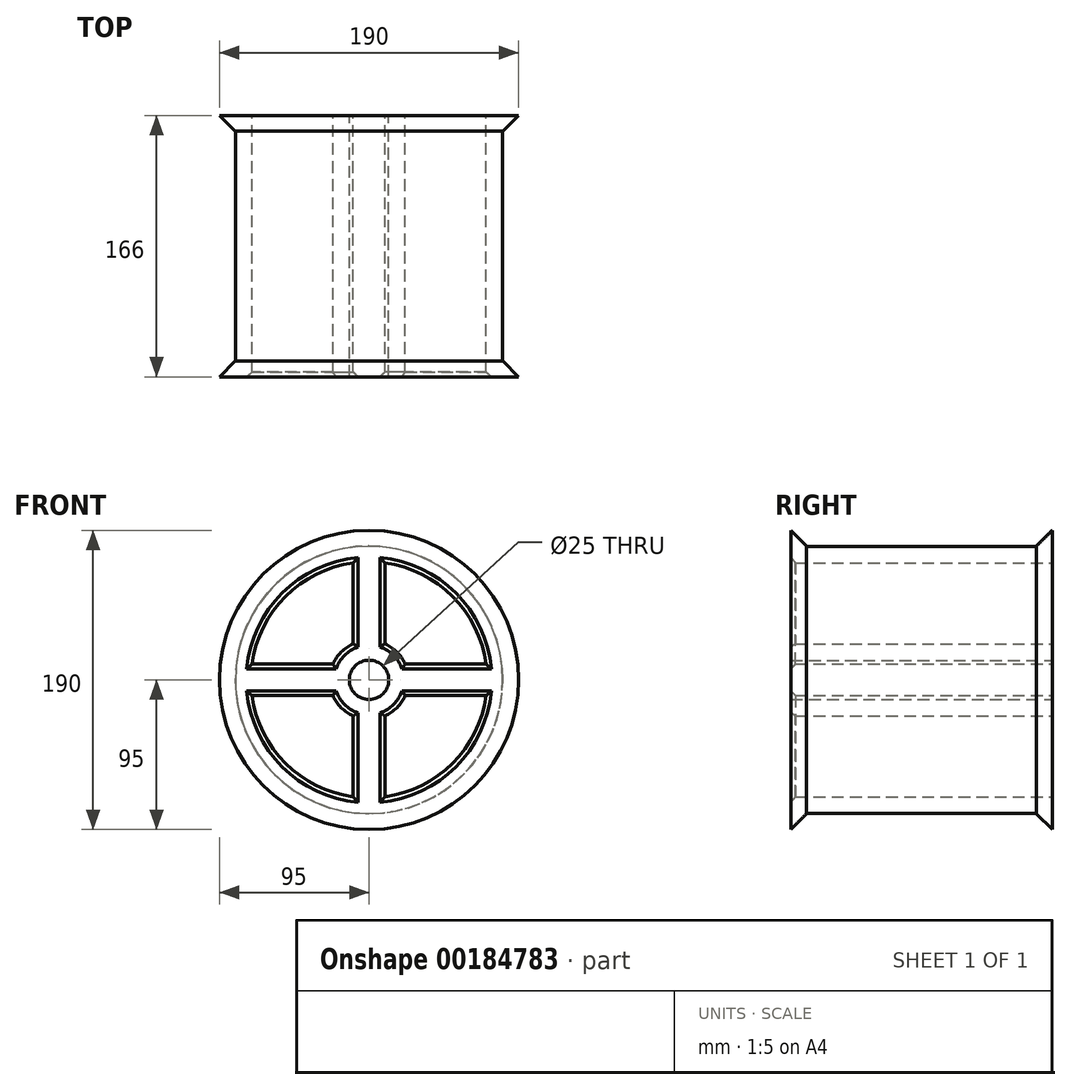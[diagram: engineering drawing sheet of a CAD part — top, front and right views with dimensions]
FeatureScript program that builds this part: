
annotation { "Feature Type Name" : "Feature", "Feature Type Description" : "" }
export const myFeature = defineFeature(function(context is Context, id is Id, definition is map)
    precondition{}
    {
        {
            var Q0;
            Q0=qCreatedBy(makeId("Front.planeOp"),FACE);
            var sketch = newSketch(context, id + "F0", { "sketchPlane" : qUnion([Q0])});
            skCircle(sketch, "E0", {"center": v(0, 0) * mm, "radius": 84.9 * mm});
            skSolve(sketch);
        }
        {
            var Q0;
            Q0=makeQuery(id+"F0.imprint","IMPRINT",FACE,{"disambiguationData":[TD([[makeQuery(id+"F0.imprint","IMPRINT",EDGE,{"derivedFrom":sQuery(id+"F0.wireOp",EDGE,"E0")}),1.0]])]});
            extrude(context, id + "F1", {"entities" : qUnion([Q0]), "depth" : 166 * mm});
        }
        {
            var Q0;
            Q0=makeQuery(id+"F1.opExtrude","CAP_FACE",FACE,{"disambiguationData":[OSD([sQuery(id+"F0.wireOp",EDGE,"E0")])],"isStart":true});
            var sketch = newSketch(context, id + "F2", { "sketchPlane" : qUnion([Q0])});
            skCircle(sketch, "E1", {"center": v(0, 0) * mm, "radius": 95 * mm});
            skSolve(sketch);
        }
        {
            var Q0;
            Q0=makeQuery(id+"F2.imprint","IMPRINT",FACE,{"disambiguationData":[TD([[makeQuery(id+"F2.imprint","IMPRINT",EDGE,{"derivedFrom":sQuery(id+"F2.wireOp",EDGE,"E1")}),1.0]])]});
            var Q1;
            Q1=sQuery(id+"F2.wireOp",EDGE,"E1");
            extrude(context, id + "F3", {"entities" : qUnion([Q0]), "operationType" : NewBodyOperationType.ADD, "surfaceEntities" : qUnion([Q1]), "oppositeDirection" : true, "depth" : 10 * mm});
        }
        {
            var Q0;
            Q0=makeQuery(id+"F1.opExtrude","CAP_FACE",FACE,{"disambiguationData":[OSD([sQuery(id+"F0.wireOp",EDGE,"E0")])],"isStart":false});
            var sketch = newSketch(context, id + "F4", { "sketchPlane" : qUnion([Q0])});
            skCircle(sketch, "E2", {"center": v(0, 0) * mm, "radius": 95 * mm});
            skSolve(sketch);
        }
        {
            var Q0;
            Q0=makeQuery(id+"F4.imprint","IMPRINT",FACE,{"disambiguationData":[TD([[makeQuery(id+"F4.imprint","IMPRINT",EDGE,{"derivedFrom":sQuery(id+"F4.wireOp",EDGE,"E2")}),1.0]])]});
            var Q1;
            Q1=sQuery(id+"F4.wireOp",EDGE,"E2");
            extrude(context, id + "F5", {"entities" : qUnion([Q0]), "operationType" : NewBodyOperationType.ADD, "surfaceEntities" : qUnion([Q1]), "oppositeDirection" : true, "depth" : 10 * mm});
        }
        {
            var Q0;
            Q0=makeQuery(id+"F3.opExtrude","CAP_EDGE",EDGE,{"disambiguationData":[OSD([sQuery(id+"F2.wireOp",EDGE,"E1")])],"isStart":false});
            var Q1;
            Q1=makeQuery(id+"F5.opExtrude","CAP_EDGE",EDGE,{"disambiguationData":[OSD([sQuery(id+"F4.wireOp",EDGE,"E2")])],"isStart":false});
            chamfer(context, id + "F6", {"entities" : qUnion([Q0, Q1]), "width" : 10 * mm, "tangentPropagation" : true});
        }
        {
            var Q0;
            {var subQ0=sQuery(id+"F0.wireOp",EDGE,"E0");Q0=makeQuery(id+"F3.boolean.opBoolean","MERGE",FACE,{"derivedFrom":[makeQuery(id+"F1.opExtrude","CAP_FACE",FACE,{"disambiguationData":[OSD([subQ0])],"isStart":true}),makeQuery(id+"F3.opExtrude","CAP_FACE",FACE,{"disambiguationData":[OSD([subQ0,sQuery(id+"F2.wireOp",EDGE,"E1")])],"isStart":true})]});}
            var sketch = newSketch(context, id + "F7", { "sketchPlane" : qUnion([Q0])});
            skCircle(sketch, "E3", {"center": v(0, 0) * mm, "radius": 75 * mm});
            skCircle(sketch, "E4", {"center": v(0, 0) * mm, "radius": 25 * mm});
            skCircle(sketch, "E5", {"center": v(0, 0) * mm, "radius": 12.5 * mm});
            skLineSegment(sketch, "E6", {"start": v(25, 0) * mm, "end": v(75, 0) * mm});
            skLineSegment(sketch, "E7", {"start": v(-25, 0) * mm, "end": v(-75, 0) * mm});
            skLineSegment(sketch, "E8", {"start": v(0, -25) * mm, "end": v(0, -75) * mm});
            skLineSegment(sketch, "E9", {"start": v(0, 25) * mm, "end": v(0, 75) * mm});
            skLineSegment(sketch, "E10", {"start": v(-22.91, 10) * mm, "end": v(-74.33, 10) * mm});
            skLineSegment(sketch, "E11", {"start": v(-22.91, -10) * mm, "end": v(-74.33, -10) * mm});
            skLineSegment(sketch, "E12", {"start": v(-10, -22.91) * mm, "end": v(-10, -74.33) * mm});
            skLineSegment(sketch, "E13", {"start": v(10, -22.91) * mm, "end": v(10, -74.33) * mm});
            skLineSegment(sketch, "E14", {"start": v(22.91, -10) * mm, "end": v(74.33, -10) * mm});
            skLineSegment(sketch, "E15", {"start": v(22.91, 10) * mm, "end": v(74.33, 10) * mm});
            skLineSegment(sketch, "E16", {"start": v(10, 22.91) * mm, "end": v(10, 74.33) * mm});
            skLineSegment(sketch, "E17", {"start": v(-10, 22.91) * mm, "end": v(-10, 74.33) * mm});
            skSolve(sketch);
        }
        {
            var Q0;
            {var subQ0=sQuery(id+"F7.wireOp",EDGE,"E10");Q0=makeQuery(id+"F7.imprint","IMPRINT",FACE,{"disambiguationData":[TD([[makeQuery(id+"F7.imprint","IMPRINT",EDGE,{"derivedFrom":subQ0}),-1.0]])]});}
            var Q1;
            {var subQ0=sQuery(id+"F7.wireOp",EDGE,"E15");Q1=makeQuery(id+"F7.imprint","IMPRINT",FACE,{"disambiguationData":[TD([[makeQuery(id+"F7.imprint","IMPRINT",EDGE,{"derivedFrom":subQ0}),1.0]])]});}
            var Q2;
            {var subQ0=sQuery(id+"F7.wireOp",EDGE,"E11");Q2=makeQuery(id+"F7.imprint","IMPRINT",FACE,{"disambiguationData":[TD([[makeQuery(id+"F7.imprint","IMPRINT",EDGE,{"derivedFrom":subQ0}),1.0]])]});}
            var Q3;
            {var subQ0=sQuery(id+"F7.wireOp",EDGE,"E13");Q3=makeQuery(id+"F7.imprint","IMPRINT",FACE,{"disambiguationData":[TD([[makeQuery(id+"F7.imprint","IMPRINT",EDGE,{"derivedFrom":subQ0}),1.0]])]});}
            var Q4;
            Q4=makeQuery(id+"F7.imprint","IMPRINT",FACE,{"disambiguationData":[TD([[makeQuery(id+"F7.imprint","IMPRINT",EDGE,{"derivedFrom":sQuery(id+"F7.wireOp",EDGE,"E5")}),1.0]])]});
            extrude(context, id + "F8", {"entities" : qUnion([Q0, Q1, Q2, Q3, Q4]), "operationType" : NewBodyOperationType.REMOVE, "endBound" : BoundingType.THROUGH_ALL, "oppositeDirection" : true, "depth" : 25.4 * mm});
        }
        {
            var Q0;
            {var subQ0=sQuery(id+"F7.wireOp",EDGE,"E3");var subQ1=sQuery(id+"F0.wireOp",EDGE,"E0");Q0=makeQuery(id+"F8.boolean.opBoolean","INTERSECT",EDGE,{"derivedFrom":[makeQuery(id+"F5.boolean.opBoolean","MERGE",FACE,{"derivedFrom":[makeQuery(id+"F1.opExtrude","CAP_FACE",FACE,{"disambiguationData":[OSD([subQ1])],"isStart":false}),makeQuery(id+"F5.opExtrude","CAP_FACE",FACE,{"disambiguationData":[OSD([subQ1,sQuery(id+"F4.wireOp",EDGE,"E2")])],"isStart":true})]}),makeQuery(id+"F8.opExtrude","SWEPT_FACE",FACE,{"disambiguationData":[OSD([subQ0]),TDD([makeQuery(id+"F7.imprint","IMPRINT",EDGE,{"disambiguationData":[TD([[makeQuery(id+"F7.imprint","INTERSECT",VERTEX,{"derivedFrom":[subQ0,sQuery(id+"F7.wireOp",EDGE,"E15")]}),-1.0]])],"derivedFrom":subQ0})])]})]});}
            var Q1;
            {var subQ0=sQuery(id+"F0.wireOp",EDGE,"E0");Q1=makeQuery(id+"F8.boolean.opBoolean","INTERSECT",EDGE,{"derivedFrom":[makeQuery(id+"F5.boolean.opBoolean","MERGE",FACE,{"derivedFrom":[makeQuery(id+"F1.opExtrude","CAP_FACE",FACE,{"disambiguationData":[OSD([subQ0])],"isStart":false}),makeQuery(id+"F5.opExtrude","CAP_FACE",FACE,{"disambiguationData":[OSD([subQ0,sQuery(id+"F4.wireOp",EDGE,"E2")])],"isStart":true})]}),makeQuery(id+"F8.opExtrude","SWEPT_FACE",FACE,{"disambiguationData":[OSD([sQuery(id+"F7.wireOp",EDGE,"E16")])]})]});}
            var Q2;
            {var subQ0=sQuery(id+"F0.wireOp",EDGE,"E0");Q2=makeQuery(id+"F8.boolean.opBoolean","INTERSECT",EDGE,{"derivedFrom":[makeQuery(id+"F5.boolean.opBoolean","MERGE",FACE,{"derivedFrom":[makeQuery(id+"F1.opExtrude","CAP_FACE",FACE,{"disambiguationData":[OSD([subQ0])],"isStart":false}),makeQuery(id+"F5.opExtrude","CAP_FACE",FACE,{"disambiguationData":[OSD([subQ0,sQuery(id+"F4.wireOp",EDGE,"E2")])],"isStart":true})]}),makeQuery(id+"F8.opExtrude","SWEPT_FACE",FACE,{"disambiguationData":[OSD([sQuery(id+"F7.wireOp",EDGE,"E15")])]})]});}
            var Q3;
            {var subQ0=sQuery(id+"F7.wireOp",EDGE,"E4");var subQ1=sQuery(id+"F0.wireOp",EDGE,"E0");Q3=makeQuery(id+"F8.boolean.opBoolean","INTERSECT",EDGE,{"derivedFrom":[makeQuery(id+"F5.boolean.opBoolean","MERGE",FACE,{"derivedFrom":[makeQuery(id+"F1.opExtrude","CAP_FACE",FACE,{"disambiguationData":[OSD([subQ1])],"isStart":false}),makeQuery(id+"F5.opExtrude","CAP_FACE",FACE,{"disambiguationData":[OSD([subQ1,sQuery(id+"F4.wireOp",EDGE,"E2")])],"isStart":true})]}),makeQuery(id+"F8.opExtrude","SWEPT_FACE",FACE,{"disambiguationData":[OSD([subQ0]),TDD([makeQuery(id+"F7.imprint","IMPRINT",EDGE,{"disambiguationData":[TD([[makeQuery(id+"F7.imprint","INTERSECT",VERTEX,{"derivedFrom":[subQ0,sQuery(id+"F7.wireOp",EDGE,"E15")]}),-1.0]])],"derivedFrom":subQ0})])]})]});}
            var Q4;
            {var subQ0=sQuery(id+"F7.wireOp",EDGE,"E3");var subQ1=sQuery(id+"F0.wireOp",EDGE,"E0");Q4=makeQuery(id+"F8.boolean.opBoolean","INTERSECT",EDGE,{"derivedFrom":[makeQuery(id+"F5.boolean.opBoolean","MERGE",FACE,{"derivedFrom":[makeQuery(id+"F1.opExtrude","CAP_FACE",FACE,{"disambiguationData":[OSD([subQ1])],"isStart":false}),makeQuery(id+"F5.opExtrude","CAP_FACE",FACE,{"disambiguationData":[OSD([subQ1,sQuery(id+"F4.wireOp",EDGE,"E2")])],"isStart":true})]}),makeQuery(id+"F8.opExtrude","SWEPT_FACE",FACE,{"disambiguationData":[OSD([subQ0]),TDD([makeQuery(id+"F7.imprint","IMPRINT",EDGE,{"disambiguationData":[TD([[makeQuery(id+"F7.imprint","INTERSECT",VERTEX,{"derivedFrom":[subQ0,sQuery(id+"F7.wireOp",EDGE,"E10")]}),1.0]])],"derivedFrom":subQ0})])]})]});}
            var Q5;
            {var subQ0=sQuery(id+"F0.wireOp",EDGE,"E0");Q5=makeQuery(id+"F8.boolean.opBoolean","INTERSECT",EDGE,{"derivedFrom":[makeQuery(id+"F5.boolean.opBoolean","MERGE",FACE,{"derivedFrom":[makeQuery(id+"F1.opExtrude","CAP_FACE",FACE,{"disambiguationData":[OSD([subQ0])],"isStart":false}),makeQuery(id+"F5.opExtrude","CAP_FACE",FACE,{"disambiguationData":[OSD([subQ0,sQuery(id+"F4.wireOp",EDGE,"E2")])],"isStart":true})]}),makeQuery(id+"F8.opExtrude","SWEPT_FACE",FACE,{"disambiguationData":[OSD([sQuery(id+"F7.wireOp",EDGE,"E10")])]})]});}
            var Q6;
            {var subQ0=sQuery(id+"F7.wireOp",EDGE,"E4");var subQ1=sQuery(id+"F0.wireOp",EDGE,"E0");Q6=makeQuery(id+"F8.boolean.opBoolean","INTERSECT",EDGE,{"derivedFrom":[makeQuery(id+"F5.boolean.opBoolean","MERGE",FACE,{"derivedFrom":[makeQuery(id+"F1.opExtrude","CAP_FACE",FACE,{"disambiguationData":[OSD([subQ1])],"isStart":false}),makeQuery(id+"F5.opExtrude","CAP_FACE",FACE,{"disambiguationData":[OSD([subQ1,sQuery(id+"F4.wireOp",EDGE,"E2")])],"isStart":true})]}),makeQuery(id+"F8.opExtrude","SWEPT_FACE",FACE,{"disambiguationData":[OSD([subQ0]),TDD([makeQuery(id+"F7.imprint","IMPRINT",EDGE,{"disambiguationData":[TD([[makeQuery(id+"F7.imprint","INTERSECT",VERTEX,{"derivedFrom":[subQ0,sQuery(id+"F7.wireOp",EDGE,"E10")]}),1.0]])],"derivedFrom":subQ0})])]})]});}
            var Q7;
            {var subQ0=sQuery(id+"F0.wireOp",EDGE,"E0");Q7=makeQuery(id+"F8.boolean.opBoolean","INTERSECT",EDGE,{"derivedFrom":[makeQuery(id+"F5.boolean.opBoolean","MERGE",FACE,{"derivedFrom":[makeQuery(id+"F1.opExtrude","CAP_FACE",FACE,{"disambiguationData":[OSD([subQ0])],"isStart":false}),makeQuery(id+"F5.opExtrude","CAP_FACE",FACE,{"disambiguationData":[OSD([subQ0,sQuery(id+"F4.wireOp",EDGE,"E2")])],"isStart":true})]}),makeQuery(id+"F8.opExtrude","SWEPT_FACE",FACE,{"disambiguationData":[OSD([sQuery(id+"F7.wireOp",EDGE,"E17")])]})]});}
            var Q8;
            {var subQ0=sQuery(id+"F0.wireOp",EDGE,"E0");Q8=makeQuery(id+"F8.boolean.opBoolean","INTERSECT",EDGE,{"derivedFrom":[makeQuery(id+"F5.boolean.opBoolean","MERGE",FACE,{"derivedFrom":[makeQuery(id+"F1.opExtrude","CAP_FACE",FACE,{"disambiguationData":[OSD([subQ0])],"isStart":false}),makeQuery(id+"F5.opExtrude","CAP_FACE",FACE,{"disambiguationData":[OSD([subQ0,sQuery(id+"F4.wireOp",EDGE,"E2")])],"isStart":true})]}),makeQuery(id+"F8.opExtrude","SWEPT_FACE",FACE,{"disambiguationData":[OSD([sQuery(id+"F7.wireOp",EDGE,"E11")])]})]});}
            var Q9;
            {var subQ0=sQuery(id+"F7.wireOp",EDGE,"E3");var subQ1=sQuery(id+"F0.wireOp",EDGE,"E0");Q9=makeQuery(id+"F8.boolean.opBoolean","INTERSECT",EDGE,{"derivedFrom":[makeQuery(id+"F5.boolean.opBoolean","MERGE",FACE,{"derivedFrom":[makeQuery(id+"F1.opExtrude","CAP_FACE",FACE,{"disambiguationData":[OSD([subQ1])],"isStart":false}),makeQuery(id+"F5.opExtrude","CAP_FACE",FACE,{"disambiguationData":[OSD([subQ1,sQuery(id+"F4.wireOp",EDGE,"E2")])],"isStart":true})]}),makeQuery(id+"F8.opExtrude","SWEPT_FACE",FACE,{"disambiguationData":[OSD([subQ0]),TDD([makeQuery(id+"F7.imprint","IMPRINT",EDGE,{"disambiguationData":[TD([[makeQuery(id+"F7.imprint","INTERSECT",VERTEX,{"derivedFrom":[subQ0,sQuery(id+"F7.wireOp",EDGE,"E11")]}),-1.0]])],"derivedFrom":subQ0})])]})]});}
            var Q10;
            {var subQ0=sQuery(id+"F7.wireOp",EDGE,"E4");var subQ1=sQuery(id+"F0.wireOp",EDGE,"E0");Q10=makeQuery(id+"F8.boolean.opBoolean","INTERSECT",EDGE,{"derivedFrom":[makeQuery(id+"F5.boolean.opBoolean","MERGE",FACE,{"derivedFrom":[makeQuery(id+"F1.opExtrude","CAP_FACE",FACE,{"disambiguationData":[OSD([subQ1])],"isStart":false}),makeQuery(id+"F5.opExtrude","CAP_FACE",FACE,{"disambiguationData":[OSD([subQ1,sQuery(id+"F4.wireOp",EDGE,"E2")])],"isStart":true})]}),makeQuery(id+"F8.opExtrude","SWEPT_FACE",FACE,{"disambiguationData":[OSD([subQ0]),TDD([makeQuery(id+"F7.imprint","IMPRINT",EDGE,{"disambiguationData":[TD([[makeQuery(id+"F7.imprint","INTERSECT",VERTEX,{"derivedFrom":[subQ0,sQuery(id+"F7.wireOp",EDGE,"E11")]}),-1.0]])],"derivedFrom":subQ0})])]})]});}
            var Q11;
            {var subQ0=sQuery(id+"F0.wireOp",EDGE,"E0");Q11=makeQuery(id+"F8.boolean.opBoolean","INTERSECT",EDGE,{"derivedFrom":[makeQuery(id+"F5.boolean.opBoolean","MERGE",FACE,{"derivedFrom":[makeQuery(id+"F1.opExtrude","CAP_FACE",FACE,{"disambiguationData":[OSD([subQ0])],"isStart":false}),makeQuery(id+"F5.opExtrude","CAP_FACE",FACE,{"disambiguationData":[OSD([subQ0,sQuery(id+"F4.wireOp",EDGE,"E2")])],"isStart":true})]}),makeQuery(id+"F8.opExtrude","SWEPT_FACE",FACE,{"disambiguationData":[OSD([sQuery(id+"F7.wireOp",EDGE,"E12")])]})]});}
            var Q12;
            {var subQ0=sQuery(id+"F0.wireOp",EDGE,"E0");Q12=makeQuery(id+"F8.boolean.opBoolean","INTERSECT",EDGE,{"derivedFrom":[makeQuery(id+"F5.boolean.opBoolean","MERGE",FACE,{"derivedFrom":[makeQuery(id+"F1.opExtrude","CAP_FACE",FACE,{"disambiguationData":[OSD([subQ0])],"isStart":false}),makeQuery(id+"F5.opExtrude","CAP_FACE",FACE,{"disambiguationData":[OSD([subQ0,sQuery(id+"F4.wireOp",EDGE,"E2")])],"isStart":true})]}),makeQuery(id+"F8.opExtrude","SWEPT_FACE",FACE,{"disambiguationData":[OSD([sQuery(id+"F7.wireOp",EDGE,"E13")])]})]});}
            var Q13;
            {var subQ0=sQuery(id+"F7.wireOp",EDGE,"E4");var subQ1=sQuery(id+"F0.wireOp",EDGE,"E0");Q13=makeQuery(id+"F8.boolean.opBoolean","INTERSECT",EDGE,{"derivedFrom":[makeQuery(id+"F5.boolean.opBoolean","MERGE",FACE,{"derivedFrom":[makeQuery(id+"F1.opExtrude","CAP_FACE",FACE,{"disambiguationData":[OSD([subQ1])],"isStart":false}),makeQuery(id+"F5.opExtrude","CAP_FACE",FACE,{"disambiguationData":[OSD([subQ1,sQuery(id+"F4.wireOp",EDGE,"E2")])],"isStart":true})]}),makeQuery(id+"F8.opExtrude","SWEPT_FACE",FACE,{"disambiguationData":[OSD([subQ0]),TDD([makeQuery(id+"F7.imprint","IMPRINT",EDGE,{"disambiguationData":[TD([[makeQuery(id+"F7.imprint","INTERSECT",VERTEX,{"derivedFrom":[subQ0,sQuery(id+"F7.wireOp",EDGE,"E13")]}),-1.0]])],"derivedFrom":subQ0})])]})]});}
            var Q14;
            {var subQ0=sQuery(id+"F0.wireOp",EDGE,"E0");Q14=makeQuery(id+"F8.boolean.opBoolean","INTERSECT",EDGE,{"derivedFrom":[makeQuery(id+"F5.boolean.opBoolean","MERGE",FACE,{"derivedFrom":[makeQuery(id+"F1.opExtrude","CAP_FACE",FACE,{"disambiguationData":[OSD([subQ0])],"isStart":false}),makeQuery(id+"F5.opExtrude","CAP_FACE",FACE,{"disambiguationData":[OSD([subQ0,sQuery(id+"F4.wireOp",EDGE,"E2")])],"isStart":true})]}),makeQuery(id+"F8.opExtrude","SWEPT_FACE",FACE,{"disambiguationData":[OSD([sQuery(id+"F7.wireOp",EDGE,"E14")])]})]});}
            var Q15;
            {var subQ0=sQuery(id+"F7.wireOp",EDGE,"E3");var subQ1=sQuery(id+"F0.wireOp",EDGE,"E0");Q15=makeQuery(id+"F8.boolean.opBoolean","INTERSECT",EDGE,{"derivedFrom":[makeQuery(id+"F5.boolean.opBoolean","MERGE",FACE,{"derivedFrom":[makeQuery(id+"F1.opExtrude","CAP_FACE",FACE,{"disambiguationData":[OSD([subQ1])],"isStart":false}),makeQuery(id+"F5.opExtrude","CAP_FACE",FACE,{"disambiguationData":[OSD([subQ1,sQuery(id+"F4.wireOp",EDGE,"E2")])],"isStart":true})]}),makeQuery(id+"F8.opExtrude","SWEPT_FACE",FACE,{"disambiguationData":[OSD([subQ0]),TDD([makeQuery(id+"F7.imprint","IMPRINT",EDGE,{"disambiguationData":[TD([[makeQuery(id+"F7.imprint","INTERSECT",VERTEX,{"derivedFrom":[subQ0,sQuery(id+"F7.wireOp",EDGE,"E13")]}),-1.0]])],"derivedFrom":subQ0})])]})]});}
            var Q16;
            {var subQ0=sQuery(id+"F7.wireOp",EDGE,"E3");Q16=makeQuery(id+"F8.boolean.opBoolean","COPY",EDGE,{"derivedFrom":makeQuery(id+"F8.opExtrude","CAP_EDGE",EDGE,{"disambiguationData":[OSD([subQ0]),TDD([makeQuery(id+"F7.imprint","IMPRINT",EDGE,{"disambiguationData":[TD([[makeQuery(id+"F7.imprint","INTERSECT",VERTEX,{"derivedFrom":[subQ0,sQuery(id+"F7.wireOp",EDGE,"E15")]}),-1.0]])],"derivedFrom":subQ0})])],"isStart":true})});}
            var Q17;
            Q17=makeQuery(id+"F8.boolean.opBoolean","COPY",EDGE,{"derivedFrom":makeQuery(id+"F8.opExtrude","CAP_EDGE",EDGE,{"disambiguationData":[OSD([sQuery(id+"F7.wireOp",EDGE,"E16")])],"isStart":true})});
            var Q18;
            {var subQ0=sQuery(id+"F7.wireOp",EDGE,"E4");Q18=makeQuery(id+"F8.boolean.opBoolean","COPY",EDGE,{"derivedFrom":makeQuery(id+"F8.opExtrude","CAP_EDGE",EDGE,{"disambiguationData":[OSD([subQ0]),TDD([makeQuery(id+"F7.imprint","IMPRINT",EDGE,{"disambiguationData":[TD([[makeQuery(id+"F7.imprint","INTERSECT",VERTEX,{"derivedFrom":[subQ0,sQuery(id+"F7.wireOp",EDGE,"E15")]}),-1.0]])],"derivedFrom":subQ0})])],"isStart":true})});}
            var Q19;
            Q19=makeQuery(id+"F8.boolean.opBoolean","COPY",EDGE,{"derivedFrom":makeQuery(id+"F8.opExtrude","CAP_EDGE",EDGE,{"disambiguationData":[OSD([sQuery(id+"F7.wireOp",EDGE,"E15")])],"isStart":true})});
            var Q20;
            {var subQ0=sQuery(id+"F7.wireOp",EDGE,"E3");Q20=makeQuery(id+"F8.boolean.opBoolean","COPY",EDGE,{"derivedFrom":makeQuery(id+"F8.opExtrude","CAP_EDGE",EDGE,{"disambiguationData":[OSD([subQ0]),TDD([makeQuery(id+"F7.imprint","IMPRINT",EDGE,{"disambiguationData":[TD([[makeQuery(id+"F7.imprint","INTERSECT",VERTEX,{"derivedFrom":[subQ0,sQuery(id+"F7.wireOp",EDGE,"E13")]}),-1.0]])],"derivedFrom":subQ0})])],"isStart":true})});}
            var Q21;
            Q21=makeQuery(id+"F8.boolean.opBoolean","COPY",EDGE,{"derivedFrom":makeQuery(id+"F8.opExtrude","CAP_EDGE",EDGE,{"disambiguationData":[OSD([sQuery(id+"F7.wireOp",EDGE,"E14")])],"isStart":true})});
            var Q22;
            {var subQ0=sQuery(id+"F7.wireOp",EDGE,"E4");Q22=makeQuery(id+"F8.boolean.opBoolean","COPY",EDGE,{"derivedFrom":makeQuery(id+"F8.opExtrude","CAP_EDGE",EDGE,{"disambiguationData":[OSD([subQ0]),TDD([makeQuery(id+"F7.imprint","IMPRINT",EDGE,{"disambiguationData":[TD([[makeQuery(id+"F7.imprint","INTERSECT",VERTEX,{"derivedFrom":[subQ0,sQuery(id+"F7.wireOp",EDGE,"E13")]}),-1.0]])],"derivedFrom":subQ0})])],"isStart":true})});}
            var Q23;
            Q23=makeQuery(id+"F8.boolean.opBoolean","COPY",EDGE,{"derivedFrom":makeQuery(id+"F8.opExtrude","CAP_EDGE",EDGE,{"disambiguationData":[OSD([sQuery(id+"F7.wireOp",EDGE,"E13")])],"isStart":true})});
            var Q24;
            Q24=makeQuery(id+"F8.boolean.opBoolean","COPY",EDGE,{"derivedFrom":makeQuery(id+"F8.opExtrude","CAP_EDGE",EDGE,{"disambiguationData":[OSD([sQuery(id+"F7.wireOp",EDGE,"E17")])],"isStart":true})});
            var Q25;
            {var subQ0=sQuery(id+"F7.wireOp",EDGE,"E3");Q25=makeQuery(id+"F8.boolean.opBoolean","COPY",EDGE,{"derivedFrom":makeQuery(id+"F8.opExtrude","CAP_EDGE",EDGE,{"disambiguationData":[OSD([subQ0]),TDD([makeQuery(id+"F7.imprint","IMPRINT",EDGE,{"disambiguationData":[TD([[makeQuery(id+"F7.imprint","INTERSECT",VERTEX,{"derivedFrom":[subQ0,sQuery(id+"F7.wireOp",EDGE,"E10")]}),1.0]])],"derivedFrom":subQ0})])],"isStart":true})});}
            var Q26;
            {var subQ0=sQuery(id+"F7.wireOp",EDGE,"E4");Q26=makeQuery(id+"F8.boolean.opBoolean","COPY",EDGE,{"derivedFrom":makeQuery(id+"F8.opExtrude","CAP_EDGE",EDGE,{"disambiguationData":[OSD([subQ0]),TDD([makeQuery(id+"F7.imprint","IMPRINT",EDGE,{"disambiguationData":[TD([[makeQuery(id+"F7.imprint","INTERSECT",VERTEX,{"derivedFrom":[subQ0,sQuery(id+"F7.wireOp",EDGE,"E10")]}),1.0]])],"derivedFrom":subQ0})])],"isStart":true})});}
            var Q27;
            Q27=makeQuery(id+"F8.boolean.opBoolean","COPY",EDGE,{"derivedFrom":makeQuery(id+"F8.opExtrude","CAP_EDGE",EDGE,{"disambiguationData":[OSD([sQuery(id+"F7.wireOp",EDGE,"E10")])],"isStart":true})});
            var Q28;
            {var subQ0=sQuery(id+"F7.wireOp",EDGE,"E4");Q28=makeQuery(id+"F8.boolean.opBoolean","COPY",EDGE,{"derivedFrom":makeQuery(id+"F8.opExtrude","CAP_EDGE",EDGE,{"disambiguationData":[OSD([subQ0]),TDD([makeQuery(id+"F7.imprint","IMPRINT",EDGE,{"disambiguationData":[TD([[makeQuery(id+"F7.imprint","INTERSECT",VERTEX,{"derivedFrom":[subQ0,sQuery(id+"F7.wireOp",EDGE,"E11")]}),-1.0]])],"derivedFrom":subQ0})])],"isStart":true})});}
            var Q29;
            Q29=makeQuery(id+"F8.boolean.opBoolean","COPY",EDGE,{"derivedFrom":makeQuery(id+"F8.opExtrude","CAP_EDGE",EDGE,{"disambiguationData":[OSD([sQuery(id+"F7.wireOp",EDGE,"E12")])],"isStart":true})});
            var Q30;
            Q30=makeQuery(id+"F8.boolean.opBoolean","COPY",EDGE,{"derivedFrom":makeQuery(id+"F8.opExtrude","CAP_EDGE",EDGE,{"disambiguationData":[OSD([sQuery(id+"F7.wireOp",EDGE,"E11")])],"isStart":true})});
            var Q31;
            {var subQ0=sQuery(id+"F7.wireOp",EDGE,"E3");Q31=makeQuery(id+"F8.boolean.opBoolean","COPY",EDGE,{"derivedFrom":makeQuery(id+"F8.opExtrude","CAP_EDGE",EDGE,{"disambiguationData":[OSD([subQ0]),TDD([makeQuery(id+"F7.imprint","IMPRINT",EDGE,{"disambiguationData":[TD([[makeQuery(id+"F7.imprint","INTERSECT",VERTEX,{"derivedFrom":[subQ0,sQuery(id+"F7.wireOp",EDGE,"E11")]}),-1.0]])],"derivedFrom":subQ0})])],"isStart":true})});}
            chamfer(context, id + "F9", {"entities" : qUnion([Q0, Q1, Q2, Q3, Q4, Q5, Q6, Q7, Q8, Q9, Q10, Q11, Q12, Q13, Q14, Q15, Q16, Q17, Q18, Q19, Q20, Q21, Q22, Q23, Q24, Q25, Q26, Q27, Q28, Q29, Q30, Q31]), "width" : 3 * mm});
        }
    });
